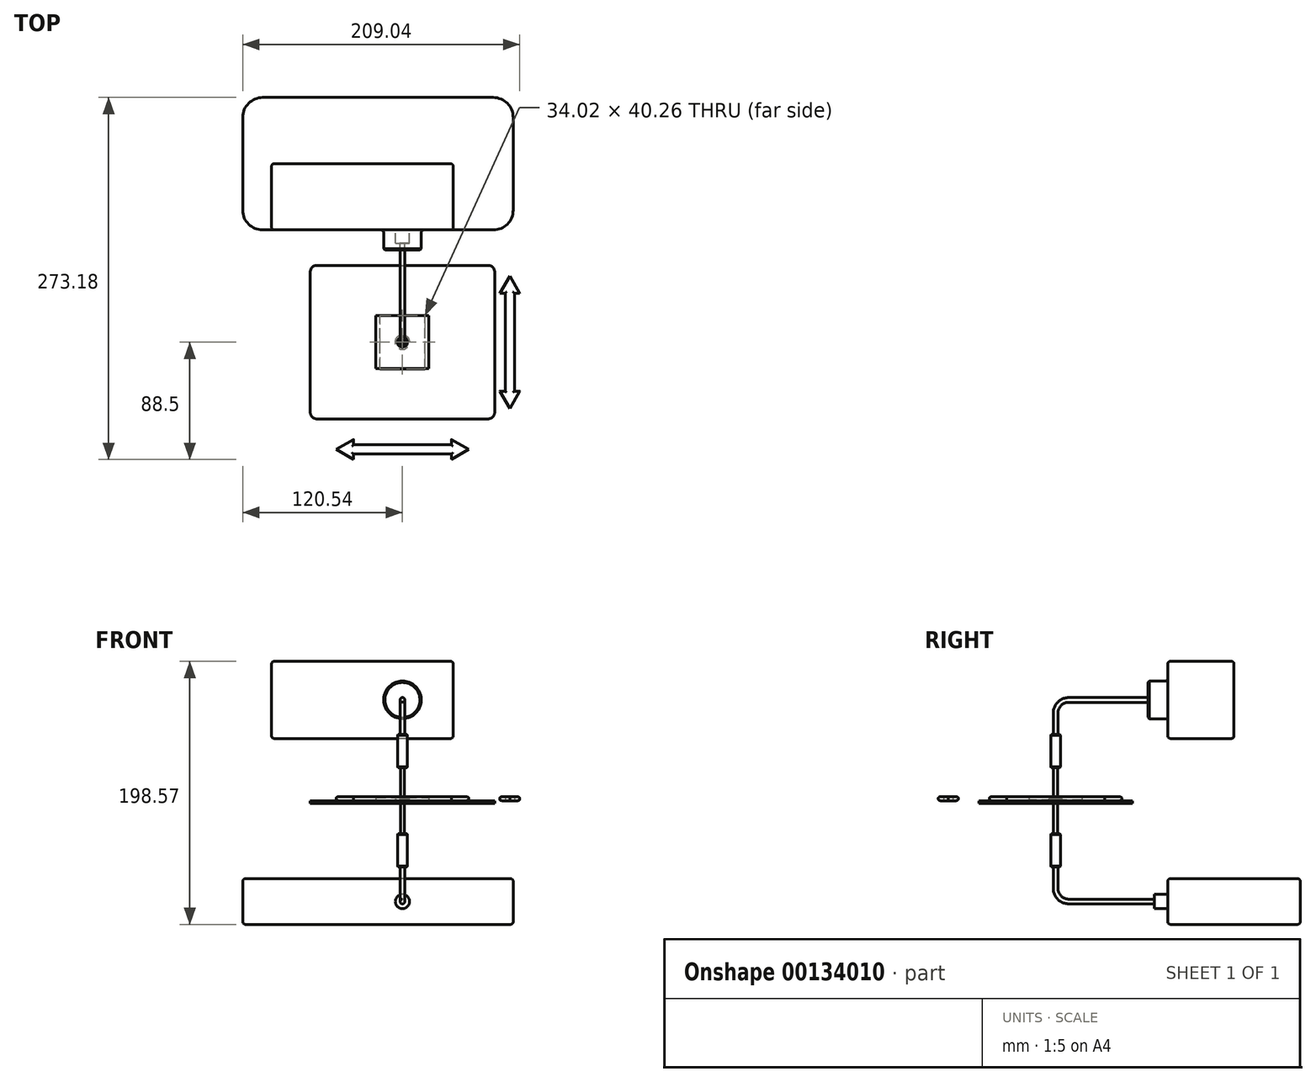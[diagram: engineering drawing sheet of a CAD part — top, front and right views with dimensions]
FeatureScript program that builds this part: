
annotation { "Feature Type Name" : "Feature", "Feature Type Description" : "" }
export const myFeature = defineFeature(function(context is Context, id is Id, definition is map)
    precondition{}
    {
        {
            var Q0;
            Q0=qCreatedBy(makeId("Top.planeOp"),FACE);
            var sketch = newSketch(context, id + "F0", { "sketchPlane" : qUnion([Q0])});
            skLineSegment(sketch, "E0.bottom", {"start": v(-64.58, 57.99) * mm, "end": v(64.58, 57.99) * mm});
            skLineSegment(sketch, "E0.top", {"start": v(-64.58, -57.99) * mm, "end": v(64.58, -57.99) * mm});
            skLineSegment(sketch, "E0.left", {"start": v(-69.58, 52.99) * mm, "end": v(-69.58, -52.99) * mm});
            skLineSegment(sketch, "E0.right", {"start": v(69.58, 52.99) * mm, "end": v(69.58, -52.99) * mm});
            skCircle(sketch, "E1", {"center": v(0, 0) * mm, "radius": 3 * mm});
            skPoint(sketch, "E2.visualSharp", {"position": v(-69.58, 57.99) * mm});
            skArc(sketch, "E2.filletArc", {"start": v(-64.58, 57.99) * mm, "mid": v(-68.12, 56.52) * mm, "end": v(-69.58, 52.99) * mm});
            skPoint(sketch, "E3.visualSharp", {"position": v(-69.58, -57.99) * mm});
            skArc(sketch, "E3.filletArc", {"start": v(-69.58, -52.99) * mm, "mid": v(-68.12, -56.52) * mm, "end": v(-64.58, -57.99) * mm});
            skPoint(sketch, "E4.visualSharp", {"position": v(69.58, -57.99) * mm});
            skArc(sketch, "E4.filletArc", {"start": v(64.58, -57.99) * mm, "mid": v(68.12, -56.52) * mm, "end": v(69.58, -52.99) * mm});
            skPoint(sketch, "E5.visualSharp", {"position": v(69.58, 57.99) * mm});
            skArc(sketch, "E5.filletArc", {"start": v(69.58, 52.99) * mm, "mid": v(68.12, 56.52) * mm, "end": v(64.58, 57.99) * mm});
            skLineSegment(sketch, "E6.bottom", {"start": v(-36.95, -77.5) * mm, "end": v(36.95, -77.5) * mm});
            skLineSegment(sketch, "E6.top", {"start": v(-36.95, -84.5) * mm, "end": v(36.95, -84.5) * mm});
            skLineSegment(sketch, "E7", {"start": v(-36.95, -77.5) * mm, "end": v(-36.95, -73.5) * mm});
            skLineSegment(sketch, "E8", {"start": v(-36.95, -73.5) * mm, "end": v(-50, -81) * mm});
            skPoint(sketch, "E8.endSnap0", {"position": v(-36.95, -81) * mm});
            skLineSegment(sketch, "E9", {"start": v(-36.95, -81) * mm, "end": v(36.95, -81) * mm, "construction": true});
            skLineSegment(sketch, "E10", {"start": v(0, -77.5) * mm, "end": v(0, -84.5) * mm, "construction": true});
            skLineSegment(sketch, "E11.MirrorCS", {"start": v(-36.95, -88.5) * mm, "end": v(-50, -81) * mm});
            skLineSegment(sketch, "E12.MirrorCS", {"start": v(-36.95, -84.5) * mm, "end": v(-36.95, -88.5) * mm});
            skLineSegment(sketch, "E13.MirrorCS", {"start": v(36.95, -77.5) * mm, "end": v(36.95, -73.5) * mm});
            skLineSegment(sketch, "E14.MirrorCS", {"start": v(36.95, -84.5) * mm, "end": v(36.95, -88.5) * mm});
            skLineSegment(sketch, "E15.MirrorCS", {"start": v(36.95, -88.5) * mm, "end": v(50, -81) * mm});
            skLineSegment(sketch, "E16.MirrorCS", {"start": v(36.95, -73.5) * mm, "end": v(50, -81) * mm});
            skPoint(sketch, "E17", {"position": v(0, -57.99) * mm});
            skLineSegment(sketch, "E18.bottom", {"start": v(17, -20.13) * mm, "end": v(-17, -20.13) * mm});
            skLineSegment(sketch, "E18.top", {"start": v(17, 20.13) * mm, "end": v(-17, 20.13) * mm});
            skLineSegment(sketch, "E18.left", {"start": v(17, -20.13) * mm, "end": v(17, 20.13) * mm});
            skLineSegment(sketch, "E18.right", {"start": v(-17, -20.13) * mm, "end": v(-17, 20.13) * mm});
            skSolve(sketch);
        }
        {
            var Q0;
            Q0=makeQuery(id+"F0.imprint","IMPRINT",FACE,{"disambiguationData":[TD([[makeQuery(id+"F0.imprint","IMPRINT",EDGE,{"derivedFrom":sQuery(id+"F0.wireOp",EDGE,"zXq7R44A-xx6G-92k3-GXYH-fsH6qLxIFY6k")}),1.0]])]});
            var Q1;
            Q1=makeQuery(id+"F0.imprint","IMPRINT",FACE,{"disambiguationData":[TD([[makeQuery(id+"F0.imprint","IMPRINT",EDGE,{"derivedFrom":sQuery(id+"F0.wireOp",EDGE,"E0.bottom")}),-1.0]])]});
            extrude(context, id + "F1", {"entities" : qUnion([Q0, Q1]), "oppositeDirection" : true, "depth" : 2 * mm});
        }
        {
            var Q0;
            Q0=makeQuery(id+"F0.imprint","IMPRINT",FACE,{"disambiguationData":[TD([[makeQuery(id+"F0.imprint","IMPRINT",EDGE,{"derivedFrom":sQuery(id+"F0.wireOp",EDGE,"E0.bottom")}),-1.0]])]});
            cPlane(context, id + "F2", {"entities" : qUnion([Q0]), "cplaneType" : CPlaneType.OFFSET, "offset" : 0.5 * mm, "width" : 150 * mm, "height" : 150 * mm});
        }
        {
            var Q0;
            Q0=qCreatedBy(id+"F2.planeOp",FACE);
            var sketch = newSketch(context, id + "F3", { "sketchPlane" : qUnion([Q0])});
            skCircle(sketch, "E19.0", {"center": v(0, 0) * mm, "radius": 3 * mm, "construction": true});
            skCircle(sketch, "E20", {"center": v(0, 0) * mm, "radius": 6.35 * mm});
            skLineSegment(sketch, "E21.bottom", {"start": v(-20, 20) * mm, "end": v(20, 20) * mm});
            skLineSegment(sketch, "E21.top", {"start": v(-20, -20) * mm, "end": v(20, -20) * mm});
            skLineSegment(sketch, "E21.left", {"start": v(-20, 20) * mm, "end": v(-20, -20) * mm});
            skLineSegment(sketch, "E21.right", {"start": v(20, 20) * mm, "end": v(20, -20) * mm});
            skCircle(sketch, "E22", {"center": v(0, 0) * mm, "radius": 12.7 * mm});
            skCircle(sketch, "E23", {"center": v(0, 0) * mm, "radius": 5 * mm});
            skCircle(sketch, "E24", {"center": v(0, 0) * mm, "radius": 11.3 * mm});
            skSolve(sketch);
        }
        {
            var Q0;
            Q0=sQuery(id+"F0.wireOp",VERTEX,"E1.center");
            var Q1;
            Q1=sQuery(id+"F0.wireOp",EDGE,"E0.left");
            cPlane(context, id + "F4", {"entities" : qUnion([Q0, Q1]), "cplaneType" : CPlaneType.LINE_POINT, "offset" : 25 * mm, "width" : 150 * mm, "height" : 150 * mm});
        }
        {
            var Q0;
            Q0=qCreatedBy(id+"F4.planeOp",FACE);
            var sketch = newSketch(context, id + "F5", { "sketchPlane" : qUnion([Q0])});
            skCircle(sketch, "E25", {"center": v(-5, 0.5) * mm, "radius": 0.5 * mm});
            skSolve(sketch);
        }
        {
            var Q0;
            Q0=makeQuery(id+"F5.imprint","IMPRINT",FACE,{"disambiguationData":[TD([[makeQuery(id+"F5.imprint","IMPRINT",EDGE,{"derivedFrom":sQuery(id+"F5.wireOp",EDGE,"E25")}),1.0]])]});
            var Q1;
            Q1=sQuery(id+"F3.wireOp",EDGE,"E20");
            sweep(context, id + "F6", {"profiles" : qUnion([Q0]), "path" : qUnion([Q1])});
        }
        {
            var Q0;
            Q0=makeQuery(id+"F3.imprint","IMPRINT",FACE,{"disambiguationData":[TD([[makeQuery(id+"F3.imprint","IMPRINT",EDGE,{"derivedFrom":sQuery(id+"F3.wireOp",EDGE,"E20")}),-1.0]])]});
            var Q1;
            Q1=makeQuery(id+"F3.imprint","IMPRINT",FACE,{"disambiguationData":[TD([[makeQuery(id+"F3.imprint","IMPRINT",EDGE,{"derivedFrom":sQuery(id+"F3.wireOp",EDGE,"E20")}),1.0]])]});
            var Q2;
            Q2=makeQuery(id+"F3.imprint","IMPRINT",FACE,{"disambiguationData":[TD([[makeQuery(id+"F3.imprint","IMPRINT",EDGE,{"derivedFrom":sQuery(id+"F3.wireOp",EDGE,"E22")}),1.0]])]});
            var Q3;
            Q3=makeQuery(id+"F3.imprint","IMPRINT",FACE,{"disambiguationData":[TD([[makeQuery(id+"F3.imprint","IMPRINT",EDGE,{"derivedFrom":sQuery(id+"F3.wireOp",EDGE,"E21.bottom")}),-1.0]])]});
            var Q4;
            Q4=makeQuery(id+"F3.imprint","IMPRINT",FACE,{"disambiguationData":[TD([[makeQuery(id+"F3.imprint","IMPRINT",EDGE,{"derivedFrom":sQuery(id+"F3.wireOp",EDGE,"E23")}),1.0]])]});
            extrude(context, id + "F7", {"entities" : qUnion([Q0, Q1, Q2, Q3, Q4]), "depth" : 2 * mm});
        }
        {
            var Q0;
            Q0=makeQuery(id+"F0.imprint","IMPRINT",FACE,{"disambiguationData":[TD([[makeQuery(id+"F0.imprint","IMPRINT",EDGE,{"derivedFrom":sQuery(id+"F0.wireOp",EDGE,"E0.bottom")}),-1.0]])]});
            cPlane(context, id + "F8", {"entities" : qUnion([Q0]), "cplaneType" : CPlaneType.OFFSET, "offset" : 25 * mm, "width" : 150 * mm, "height" : 150 * mm});
        }
        {
            var Q0;
            Q0=qCreatedBy(id+"F8.planeOp",FACE);
            var sketch = newSketch(context, id + "F9", { "sketchPlane" : qUnion([Q0])});
            skCircle(sketch, "E26", {"center": v(0, 0) * mm, "radius": 3.7 * mm});
            skCircle(sketch, "E27", {"center": v(0, 0) * mm, "radius": 1.53 * mm});
            skSolve(sketch);
        }
        {
            var Q0;
            Q0=makeQuery(id+"F9.imprint","IMPRINT",FACE,{"disambiguationData":[TD([[makeQuery(id+"F9.imprint","IMPRINT",EDGE,{"derivedFrom":sQuery(id+"F9.wireOp",EDGE,"E26")}),1.0]])]});
            var Q1;
            Q1=makeQuery(id+"F9.imprint","IMPRINT",FACE,{"disambiguationData":[TD([[makeQuery(id+"F9.imprint","IMPRINT",EDGE,{"derivedFrom":sQuery(id+"F9.wireOp",EDGE,"E27")}),1.0]])]});
            var Q2;
            Q2=sQuery(id+"F9.wireOp",EDGE,"E26");
            extrude(context, id + "F10", {"entities" : qUnion([Q0, Q1]), "surfaceEntities" : qUnion([Q2]), "depth" : 25 * mm});
        }
        {
            var Q0;
            Q0=makeQuery(id+"F9.imprint","IMPRINT",FACE,{"disambiguationData":[TD([[makeQuery(id+"F9.imprint","IMPRINT",EDGE,{"derivedFrom":sQuery(id+"F9.wireOp",EDGE,"E27")}),1.0]])]});
            extrude(context, id + "F11", {"entities" : qUnion([Q0]), "oppositeDirection" : true, "depth" : 50 * mm});
        }
        {
            var Q0;
            Q0=makeQuery(id+"F10.opExtrude","SWEPT_FACE",FACE,{"disambiguationData":[OSD([sQuery(id+"F9.wireOp",EDGE,"E26")])]});
            chamfer(context, id + "F12", {"entities" : qUnion([Q0]), "width" : 0.5 * mm, "tangentPropagation" : true});
        }
        {
            var Q0;
            Q0=qCreatedBy(makeId("Right.planeOp"),FACE);
            var sketch = newSketch(context, id + "F13", { "sketchPlane" : qUnion([Q0])});
            skLineSegment(sketch, "E28", {"start": v(-3.7, 25.5) * mm, "end": v(-3.7, 49.5) * mm, "construction": true});
            skLineSegment(sketch, "E29", {"start": v(3.7, 49.5) * mm, "end": v(3.7, 25.5) * mm, "construction": true});
            skLineSegment(sketch, "E30", {"start": v(0, 49.5) * mm, "end": v(0, 66.09) * mm});
            skLineSegment(sketch, "E31", {"start": v(10, 76.09) * mm, "end": v(84.68, 76.09) * mm});
            skPoint(sketch, "E32.visualSharp", {"position": v(0, 76.09) * mm});
            skArc(sketch, "E32.filletArc", {"start": v(10, 76.09) * mm, "mid": v(2.93, 73.16) * mm, "end": v(0, 66.09) * mm});
            skSolve(sketch);
        }
        {
            var Q0;
            Q0=makeQuery(id+"F10.opExtrude","CAP_FACE",FACE,{"disambiguationData":[OSD([sQuery(id+"F9.wireOp",EDGE,"E26")])],"isStart":false});
            var sketch = newSketch(context, id + "F14", { "sketchPlane" : qUnion([Q0])});
            skCircle(sketch, "E33", {"center": v(0, 0) * mm, "radius": 1.78 * mm});
            skSolve(sketch);
        }
        {
            var Q0;
            Q0=makeQuery(id+"F14.imprint","IMPRINT",FACE,{"disambiguationData":[TD([[makeQuery(id+"F14.imprint","IMPRINT",EDGE,{"derivedFrom":sQuery(id+"F14.wireOp",EDGE,"E33")}),1.0]])]});
            var Q1;
            Q1=sQuery(id+"F13.wireOp",EDGE,"E30");
            var Q2;
            Q2=sQuery(id+"F13.wireOp",EDGE,"E32.filletArc");
            var Q3;
            Q3=sQuery(id+"F13.wireOp",EDGE,"E31");
            sweep(context, id + "F15", {"profiles" : qUnion([Q0]), "path" : qUnion([Q1, Q2, Q3])});
        }
        {
            var Q0;
            Q0=makeQuery(id+"F10.opExtrude","SWEPT_BODY",BODY,{"disambiguationData":[OSD([sQuery(id+"F9.wireOp",EDGE,"E26")])]});
            var Q1;
            Q1=makeQuery(id+"F15.opSweep","SWEPT_BODY",BODY,{"disambiguationData":[OSD([sQuery(id+"F13.wireOp",EDGE,"E31"),sQuery(id+"F14.wireOp",EDGE,"E33")])]});
            var Q2;
            Q2=makeQuery(id+"F0.imprint","IMPRINT",FACE,{"disambiguationData":[TD([[makeQuery(id+"F0.imprint","IMPRINT",EDGE,{"derivedFrom":sQuery(id+"F0.wireOp",EDGE,"E0.bottom")}),-1.0]])]});
            mirror(context, id + "F16", {"entities" : qUnion([Q0, Q1]), "mirrorPlane" : qUnion([Q2])});
        }
        {
            var Q0;
            Q0=makeQuery(id+"F15.opSweep","CAP_FACE",FACE,{"disambiguationData":[OSD([sQuery(id+"F13.wireOp",VERTEX,"E31.end"),sQuery(id+"F14.wireOp",EDGE,"E33")])],"isStart":false});
            var sketch = newSketch(context, id + "F17", { "sketchPlane" : qUnion([Q0])});
            skCircle(sketch, "E34.0", {"center": v(0, 76.09) * mm, "radius": 1.78 * mm, "construction": true});
            skCircle(sketch, "E35.0", {"center": v(0, -76.09) * mm, "radius": 1.78 * mm, "construction": true});
            skLineSegment(sketch, "E36.bottom", {"start": v(-38.34, 105.2) * mm, "end": v(98.82, 105.2) * mm});
            skLineSegment(sketch, "E36.top", {"start": v(-38.34, 46.97) * mm, "end": v(98.82, 46.97) * mm});
            skLineSegment(sketch, "E36.left", {"start": v(-38.34, 105.2) * mm, "end": v(-38.34, 46.97) * mm});
            skLineSegment(sketch, "E36.right", {"start": v(98.82, 105.2) * mm, "end": v(98.82, 46.97) * mm});
            skLineSegment(sketch, "E37.bottom", {"start": v(-83.57, -58.81) * mm, "end": v(120.54, -58.81) * mm});
            skLineSegment(sketch, "E37.top", {"start": v(-83.57, -93.36) * mm, "end": v(120.54, -93.36) * mm});
            skLineSegment(sketch, "E37.left", {"start": v(-83.57, -58.81) * mm, "end": v(-83.57, -93.36) * mm});
            skLineSegment(sketch, "E37.right", {"start": v(120.54, -58.81) * mm, "end": v(120.54, -93.36) * mm});
            skCircle(sketch, "E38", {"center": v(0, 76.09) * mm, "radius": 14.18 * mm});
            skCircle(sketch, "E39", {"center": v(0, -76.09) * mm, "radius": 5.39 * mm});
            skPoint(sketch, "E40", {"position": v(-83.57, -76.09) * mm});
            skPoint(sketch, "E41", {"position": v(-38.34, 76.09) * mm});
            skSolve(sketch);
        }
        {
            var Q0;
            Q0=makeQuery(id+"F17.imprint","IMPRINT",FACE,{"disambiguationData":[TD([[makeQuery(id+"F17.imprint","IMPRINT",EDGE,{"derivedFrom":sQuery(id+"F17.wireOp",EDGE,"E36.bottom")}),-1.0]])]});
            var Q1;
            Q1=makeQuery(id+"F17.imprint","IMPRINT",FACE,{"disambiguationData":[TD([[makeQuery(id+"F17.imprint","IMPRINT",EDGE,{"derivedFrom":sQuery(id+"F17.wireOp",EDGE,"E38")}),1.0]])]});
            var Q2;
            Q2=makeQuery(id+"F17.imprint","IMPRINT",FACE,{"disambiguationData":[TD([[makeQuery(id+"F17.imprint","IMPRINT",EDGE,{"derivedFrom":makeQuery(id+"F15.opSweep","CAP_EDGE",EDGE,{"disambiguationData":[OSD([sQuery(id+"F13.wireOp",VERTEX,"E31.end"),sQuery(id+"F14.wireOp",EDGE,"E33")])],"isStart":false})}),1.0]])]});
            extrude(context, id + "F18", {"entities" : qUnion([Q0, Q1, Q2]), "depth" : 50 * mm});
        }
        {
            var Q0;
            Q0=makeQuery(id+"F17.imprint","IMPRINT",FACE,{"disambiguationData":[TD([[makeQuery(id+"F17.imprint","IMPRINT",EDGE,{"derivedFrom":sQuery(id+"F17.wireOp",EDGE,"E38")}),1.0]])]});
            extrude(context, id + "F19", {"entities" : qUnion([Q0]), "operationType" : NewBodyOperationType.ADD, "oppositeDirection" : true, "depth" : 15 * mm});
        }
        {
            var Q0;
            Q0=makeQuery(id+"F17.imprint","IMPRINT",FACE,{"disambiguationData":[TD([[makeQuery(id+"F17.imprint","IMPRINT",EDGE,{"derivedFrom":sQuery(id+"F17.wireOp",EDGE,"E37.bottom")}),-1.0]])]});
            var Q1;
            Q1=makeQuery(id+"F17.imprint","IMPRINT",FACE,{"disambiguationData":[TD([[makeQuery(id+"F17.imprint","IMPRINT",EDGE,{"derivedFrom":sQuery(id+"F17.wireOp",EDGE,"E39")}),1.0]])]});
            extrude(context, id + "F20", {"entities" : qUnion([Q0, Q1]), "depth" : 100 * mm});
        }
        {
            var Q0;
            Q0=makeQuery(id+"F17.imprint","IMPRINT",FACE,{"disambiguationData":[TD([[makeQuery(id+"F17.imprint","IMPRINT",EDGE,{"derivedFrom":sQuery(id+"F17.wireOp",EDGE,"E39")}),1.0]])]});
            var Q1;
            Q1=sQuery(id+"F17.wireOp",EDGE,"E39");
            extrude(context, id + "F21", {"entities" : qUnion([Q0]), "operationType" : NewBodyOperationType.ADD, "surfaceEntities" : qUnion([Q1]), "oppositeDirection" : true, "depth" : 10 * mm});
        }
        {
            var Q0;
            Q0=makeQuery(id+"F20.opExtrude","CAP_EDGE",EDGE,{"disambiguationData":[OSD([sQuery(id+"F17.wireOp",EDGE,"E37.left")])],"isStart":false});
            var Q1;
            Q1=makeQuery(id+"F20.opExtrude","CAP_EDGE",EDGE,{"disambiguationData":[OSD([sQuery(id+"F17.wireOp",EDGE,"E37.right")])],"isStart":false});
            var Q2;
            Q2=makeQuery(id+"F20.opExtrude","CAP_EDGE",EDGE,{"disambiguationData":[OSD([sQuery(id+"F17.wireOp",EDGE,"E37.right")])],"isStart":true});
            var Q3;
            Q3=makeQuery(id+"F20.opExtrude","CAP_EDGE",EDGE,{"disambiguationData":[OSD([sQuery(id+"F17.wireOp",EDGE,"E37.left")])],"isStart":true});
            fillet(context, id + "F22", {"entities" : qUnion([Q0, Q1, Q2, Q3]), "radius" : 15 * mm, "tangentPropagation" : true, "allowEdgeOverflow" : false});
        }
        {
            var Q0;
            Q0=makeQuery(id+"F20.opExtrude","SWEPT_FACE",FACE,{"disambiguationData":[OSD([sQuery(id+"F17.wireOp",EDGE,"E37.bottom")])]});
            var Q1;
            Q1=makeQuery(id+"F20.opExtrude","SWEPT_FACE",FACE,{"disambiguationData":[OSD([sQuery(id+"F17.wireOp",EDGE,"E37.top")])]});
            var Q2;
            {var subQ0=sQuery(id+"F17.wireOp",EDGE,"E36.right");var subQ1=sQuery(id+"F17.wireOp",EDGE,"E36.bottom");var subQ2=sQuery(id+"F17.wireOp",EDGE,"E36.top");var subQ3=sQuery(id+"F17.wireOp",EDGE,"E36.left");Q2=makeQuery(id+"F19.boolean.opBoolean","SPLIT",FACE,{"disambiguationData":[TD([makeQuery(id+"F18.opExtrude","SWEPT_FACE",FACE,{"disambiguationData":[OSD([subQ1])]})])],"derivedFrom":makeQuery(id+"F18.opExtrude","CAP_FACE",FACE,{"disambiguationData":[OSD([subQ1,subQ2,subQ3,subQ0])],"isStart":true})});}
            var Q3;
            Q3=makeQuery(id+"F18.opExtrude","CAP_FACE",FACE,{"disambiguationData":[OSD([sQuery(id+"F17.wireOp",EDGE,"E36.bottom"),sQuery(id+"F17.wireOp",EDGE,"E36.top"),sQuery(id+"F17.wireOp",EDGE,"E36.left"),sQuery(id+"F17.wireOp",EDGE,"E36.right")])],"isStart":false});
            var Q4;
            Q4=makeQuery(id+"F18.opExtrude","SWEPT_FACE",FACE,{"disambiguationData":[OSD([sQuery(id+"F17.wireOp",EDGE,"E36.left")])]});
            var Q5;
            Q5=makeQuery(id+"F18.opExtrude","SWEPT_FACE",FACE,{"disambiguationData":[OSD([sQuery(id+"F17.wireOp",EDGE,"E36.right")])]});
            fillet(context, id + "F23", {"entities" : qUnion([Q0, Q1, Q2, Q3, Q4, Q5]), "radius" : 2 * mm, "tangentPropagation" : true, "allowEdgeOverflow" : false});
        }
        {
            var Q0;
            Q0=makeQuery(id+"F19.opExtrude","CAP_EDGE",EDGE,{"disambiguationData":[OSD([sQuery(id+"F17.wireOp",EDGE,"E38")])],"isStart":false});
            chamfer(context, id + "F24", {"entities" : qUnion([Q0]), "width" : 1 * mm, "tangentPropagation" : true});
        }
        {
            var Q0;
            Q0=makeQuery(id+"F0.imprint","IMPRINT",FACE,{"disambiguationData":[TD([[makeQuery(id+"F0.imprint","IMPRINT",EDGE,{"derivedFrom":sQuery(id+"F0.wireOp",EDGE,"E6.bottom")}),-1.0]])]});
            extrude(context, id + "F25", {"entities" : qUnion([Q0]), "depth" : 3 * mm});
        }
        {
            var Q0;
            Q0=makeQuery(id+"F25.opExtrude","SWEPT_BODY",BODY,{"disambiguationData":[OSD([sQuery(id+"F0.wireOp",EDGE,"E6.bottom"),sQuery(id+"F0.wireOp",EDGE,"E6.top"),sQuery(id+"F0.wireOp",EDGE,"E7"),sQuery(id+"F0.wireOp",EDGE,"E8"),sQuery(id+"F0.wireOp",EDGE,"E11.MirrorCS"),sQuery(id+"F0.wireOp",EDGE,"E12.MirrorCS"),sQuery(id+"F0.wireOp",EDGE,"E13.MirrorCS"),sQuery(id+"F0.wireOp",EDGE,"E14.MirrorCS"),sQuery(id+"F0.wireOp",EDGE,"E15.MirrorCS"),sQuery(id+"F0.wireOp",EDGE,"E16.MirrorCS")])]});
            var Q1;
            Q1=makeQuery(id+"F11.opExtrude","SWEPT_FACE",FACE,{"disambiguationData":[OSD([sQuery(id+"F9.wireOp",EDGE,"E27")])]});
            transform(context, id + "F26", {"entities" : qUnion([Q0]), "transformType" : TransformType.ROTATION, "transformAxis" : qUnion([Q1]), "angle" : 90 * degree, "makeCopy" : true});
        }
        {
            var Q0;
            Q0=makeQuery(id+"F25.opExtrude","CAP_FACE",FACE,{"disambiguationData":[OSD([sQuery(id+"F0.wireOp",EDGE,"E6.bottom"),sQuery(id+"F0.wireOp",EDGE,"E6.top"),sQuery(id+"F0.wireOp",EDGE,"E7"),sQuery(id+"F0.wireOp",EDGE,"E8"),sQuery(id+"F0.wireOp",EDGE,"E11.MirrorCS"),sQuery(id+"F0.wireOp",EDGE,"E12.MirrorCS"),sQuery(id+"F0.wireOp",EDGE,"E13.MirrorCS"),sQuery(id+"F0.wireOp",EDGE,"E14.MirrorCS"),sQuery(id+"F0.wireOp",EDGE,"E15.MirrorCS"),sQuery(id+"F0.wireOp",EDGE,"E16.MirrorCS")])],"isStart":false});
            var Q1;
            Q1=makeQuery(id+"F25.opExtrude","CAP_FACE",FACE,{"disambiguationData":[OSD([sQuery(id+"F0.wireOp",EDGE,"E6.bottom"),sQuery(id+"F0.wireOp",EDGE,"E6.top"),sQuery(id+"F0.wireOp",EDGE,"E7"),sQuery(id+"F0.wireOp",EDGE,"E8"),sQuery(id+"F0.wireOp",EDGE,"E11.MirrorCS"),sQuery(id+"F0.wireOp",EDGE,"E12.MirrorCS"),sQuery(id+"F0.wireOp",EDGE,"E13.MirrorCS"),sQuery(id+"F0.wireOp",EDGE,"E14.MirrorCS"),sQuery(id+"F0.wireOp",EDGE,"E15.MirrorCS"),sQuery(id+"F0.wireOp",EDGE,"E16.MirrorCS")])],"isStart":true});
            var Q2;
            Q2=makeQuery(id+"F26.opPattern","COPY",FACE,{"derivedFrom":makeQuery(id+"F25.opExtrude","CAP_FACE",FACE,{"disambiguationData":[OSD([sQuery(id+"F0.wireOp",EDGE,"E6.bottom"),sQuery(id+"F0.wireOp",EDGE,"E6.top"),sQuery(id+"F0.wireOp",EDGE,"E7"),sQuery(id+"F0.wireOp",EDGE,"E8"),sQuery(id+"F0.wireOp",EDGE,"E11.MirrorCS"),sQuery(id+"F0.wireOp",EDGE,"E12.MirrorCS"),sQuery(id+"F0.wireOp",EDGE,"E13.MirrorCS"),sQuery(id+"F0.wireOp",EDGE,"E14.MirrorCS"),sQuery(id+"F0.wireOp",EDGE,"E15.MirrorCS"),sQuery(id+"F0.wireOp",EDGE,"E16.MirrorCS")])],"isStart":true}),"instanceName":"1"});
            var Q3;
            Q3=makeQuery(id+"F26.opPattern","COPY",FACE,{"derivedFrom":makeQuery(id+"F25.opExtrude","CAP_FACE",FACE,{"disambiguationData":[OSD([sQuery(id+"F0.wireOp",EDGE,"E6.bottom"),sQuery(id+"F0.wireOp",EDGE,"E6.top"),sQuery(id+"F0.wireOp",EDGE,"E7"),sQuery(id+"F0.wireOp",EDGE,"E8"),sQuery(id+"F0.wireOp",EDGE,"E11.MirrorCS"),sQuery(id+"F0.wireOp",EDGE,"E12.MirrorCS"),sQuery(id+"F0.wireOp",EDGE,"E13.MirrorCS"),sQuery(id+"F0.wireOp",EDGE,"E14.MirrorCS"),sQuery(id+"F0.wireOp",EDGE,"E15.MirrorCS"),sQuery(id+"F0.wireOp",EDGE,"E16.MirrorCS")])],"isStart":false}),"instanceName":"1"});
            fillet(context, id + "F27", {"entities" : qUnion([Q0, Q1, Q2, Q3]), "radius" : 1 * mm, "tangentPropagation" : true, "allowEdgeOverflow" : false});
        }
    });
